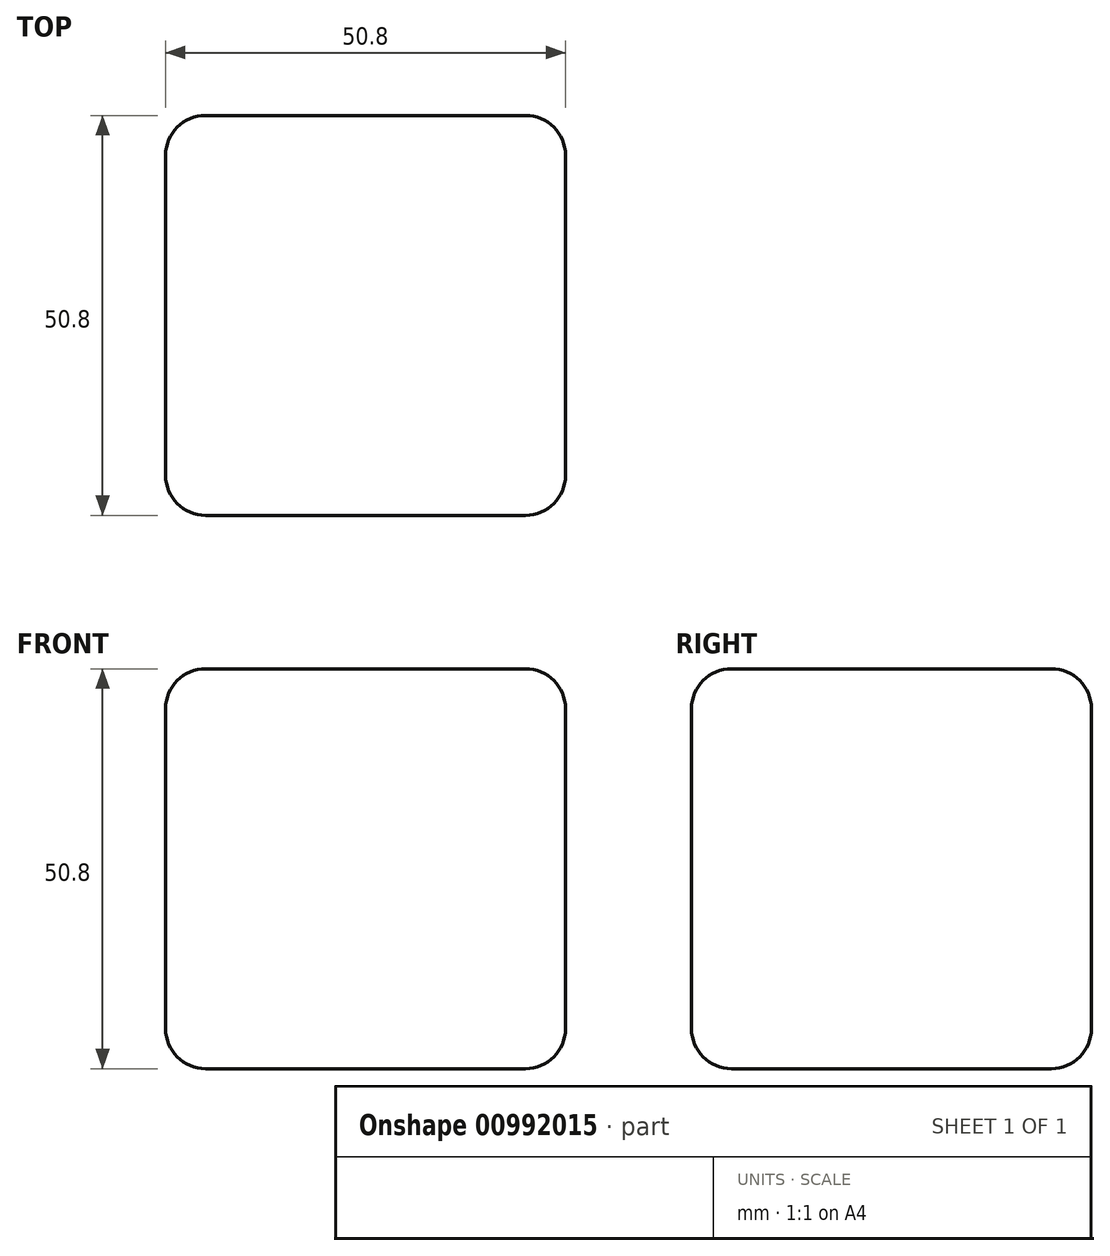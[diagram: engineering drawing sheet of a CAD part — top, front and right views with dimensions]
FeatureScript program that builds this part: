
annotation { "Feature Type Name" : "Feature", "Feature Type Description" : "" }
export const myFeature = defineFeature(function(context is Context, id is Id, definition is map)
    precondition{}
    {
        {
            var Q0;
            Q0=qCreatedBy(makeId("Front.planeOp"),FACE);
            var sketch = newSketch(context, id + "F0", { "sketchPlane" : qUnion([Q0])});
            skLineSegment(sketch, "E0.bottom", {"start": v(25.4, 25.4) * mm, "end": v(-25.4, 25.4) * mm});
            skLineSegment(sketch, "E0.top", {"start": v(25.4, -25.4) * mm, "end": v(-25.4, -25.4) * mm});
            skLineSegment(sketch, "E0.left", {"start": v(25.4, 25.4) * mm, "end": v(25.4, -25.4) * mm});
            skLineSegment(sketch, "E0.right", {"start": v(-25.4, 25.4) * mm, "end": v(-25.4, -25.4) * mm});
            skPoint(sketch, "E0.middle", {"position": v(0, 0) * mm});
            skSolve(sketch);
        }
        {
            var Q0;
            Q0 = qSketchRegion(id + "F0", true);
            extrude(context, id + "F1", {"entities" : qUnion([Q0]), "depth" : 50.8 * mm, "offsetDistance" : 25.4 * mm});
        }
        {
            var Q0;
            Q0=makeQuery(id+"F1.opExtrude","CAP_EDGE",EDGE,{"disambiguationData":[OSD([sQuery(id+"F0.wireOp",EDGE,"E0.bottom")])],"isStart":false});
            var Q1;
            Q1=makeQuery(id+"F1.opExtrude","SWEPT_EDGE",EDGE,{"disambiguationData":[OSD([sQuery(id+"F0.wireOp",EDGE,"E0.bottom"),sQuery(id+"F0.wireOp",EDGE,"E0.left")])]});
            var Q2;
            Q2=makeQuery(id+"F1.opExtrude","CAP_EDGE",EDGE,{"disambiguationData":[OSD([sQuery(id+"F0.wireOp",EDGE,"E0.bottom")])],"isStart":true});
            var Q3;
            Q3=makeQuery(id+"F1.opExtrude","SWEPT_EDGE",EDGE,{"disambiguationData":[OSD([sQuery(id+"F0.wireOp",EDGE,"E0.bottom"),sQuery(id+"F0.wireOp",EDGE,"E0.right")])]});
            var Q4;
            Q4=makeQuery(id+"F1.opExtrude","CAP_EDGE",EDGE,{"disambiguationData":[OSD([sQuery(id+"F0.wireOp",EDGE,"E0.left")])],"isStart":true});
            var Q5;
            Q5=makeQuery(id+"F1.opExtrude","CAP_EDGE",EDGE,{"disambiguationData":[OSD([sQuery(id+"F0.wireOp",EDGE,"E0.left")])],"isStart":false});
            var Q6;
            Q6=makeQuery(id+"F1.opExtrude","CAP_EDGE",EDGE,{"disambiguationData":[OSD([sQuery(id+"F0.wireOp",EDGE,"E0.right")])],"isStart":false});
            var Q7;
            Q7=makeQuery(id+"F1.opExtrude","CAP_EDGE",EDGE,{"disambiguationData":[OSD([sQuery(id+"F0.wireOp",EDGE,"E0.top")])],"isStart":false});
            var Q8;
            Q8=makeQuery(id+"F1.opExtrude","SWEPT_EDGE",EDGE,{"disambiguationData":[OSD([sQuery(id+"F0.wireOp",EDGE,"E0.top"),sQuery(id+"F0.wireOp",EDGE,"E0.left")])]});
            var Q9;
            Q9=makeQuery(id+"F1.opExtrude","SWEPT_EDGE",EDGE,{"disambiguationData":[OSD([sQuery(id+"F0.wireOp",EDGE,"E0.top"),sQuery(id+"F0.wireOp",EDGE,"E0.right")])]});
            var Q10;
            Q10=makeQuery(id+"F1.opExtrude","CAP_EDGE",EDGE,{"disambiguationData":[OSD([sQuery(id+"F0.wireOp",EDGE,"E0.top")])],"isStart":true});
            var Q11;
            Q11=makeQuery(id+"F1.opExtrude","CAP_EDGE",EDGE,{"disambiguationData":[OSD([sQuery(id+"F0.wireOp",EDGE,"E0.right")])],"isStart":true});
            fillet(context, id + "F2", {"entities" : qUnion([Q0, Q1, Q2, Q3, Q4, Q5, Q6, Q7, Q8, Q9, Q10, Q11]), "radius" : 5.08 * mm, "tangentPropagation" : true, "allowEdgeOverflow" : false});
        }
    });
